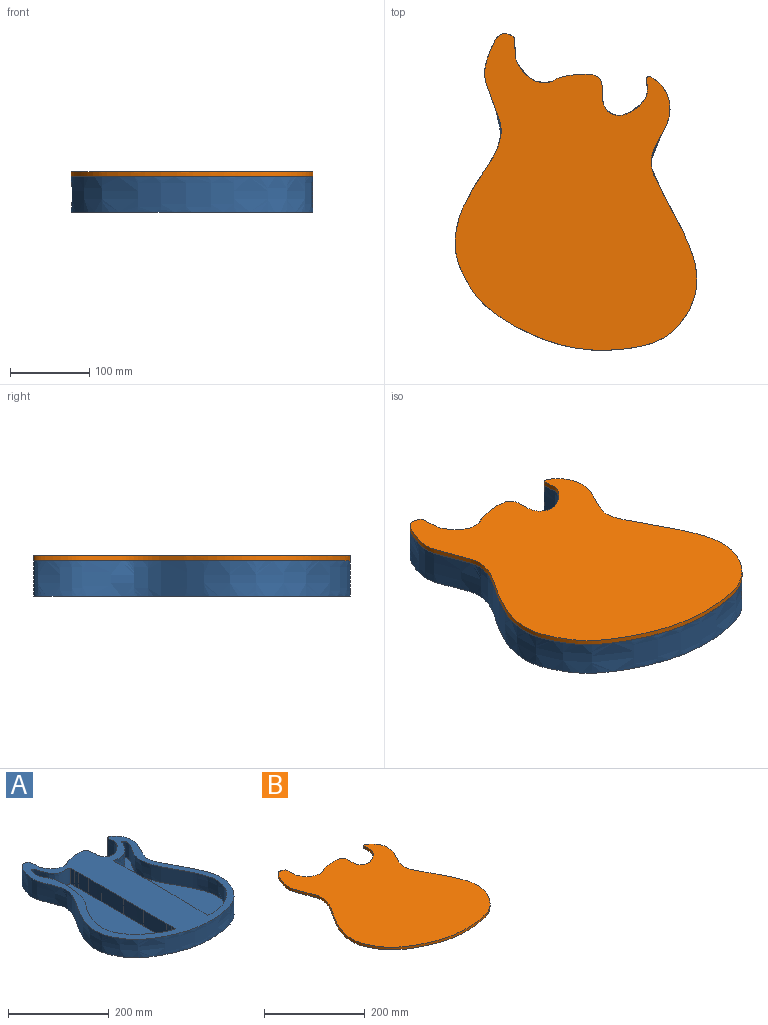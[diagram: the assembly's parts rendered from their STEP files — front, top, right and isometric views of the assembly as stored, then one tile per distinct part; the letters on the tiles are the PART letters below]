
ASSEMBLY  parts=2 mates=1
PART A: 21 faces, bbox 309.7x404x44.5 mm
  f0: plane 403.97x309.73mm, normal (0,0,1), area 41855.9mm2, adj f1,f3,f4,f5,f6,f7,f8,f10
  f1: extruded ~396.77x305.5mm, area 57898.6mm2, adj f0,f2
  f2: plane 403.97x309.73mm, normal (0,0,-1), area 81380.2mm2, adj f1
  f3: extruded ~38.1x13.88mm, area 530.3mm2, adj f0,f4,f8,f9
  f4: plane 38.1x11.9mm, normal (1,0,0), area 453.3mm2, adj f0,f3,f5,f9
  f5: extruded ~300.85x97.77mm, area 17424.5mm2, adj f0,f4,f6,f9
  f6: plane 38.1x23.8mm, normal (1,0,0), area 906.7mm2, adj f0,f5,f7,f9
  f7: extruded ~203.27x38.1mm, area 7747.2mm2, adj f0,f6,f8,f9
  f8: plane 38.1x9.92mm, normal (1,0,0), area 377.8mm2, adj f0,f3,f7,f9
  f9: plane 306.38x100.36mm, normal (0,0,1), area 18350.1mm2, adj f3,f4,f5,f6,f7,f8
  f10: plane 38.1x10.91mm, normal (-1,0,0), area 415.6mm2, adj f0,f11,f19,f20
  f11: extruded ~38.1x11.9mm, area 455.2mm2, adj f0,f10,f12,f20
  f12: plane 64.45x38.1mm, normal (-1,0,0), area 2455.6mm2, adj f0,f11,f13,f20
  f13: extruded ~56.88x38.1mm, area 2167.2mm2, adj f0,f12,f14,f20
  f14: plane 63.1x38.1mm, normal (-1,0,0), area 2404mm2, adj f0,f13,f15,f20
  f15: extruded ~38.1x35.52mm, area 1353.2mm2, adj f0,f14,f16,f20
  f16: plane 38.1x28.35mm, normal (-1,0,0), area 1080.3mm2, adj f0,f15,f17,f20
  f17: extruded ~38.1x10.13mm, area 387mm2, adj f0,f16,f18,f20
  f18: plane 38.1x11.28mm, normal (-1,0,0), area 429.7mm2, adj f0,f17,f19,f20
  f19: extruded ~344.12x100.4mm, area 18794.2mm2, adj f0,f10,f18,f20
  f20: plane 355.89x106.71mm, normal (0,0,1), area 21140.1mm2, adj f10,f11,f12,f13,f14,f15,f16,f17
PART B: 3 faces, bbox 309.7x404x6.4 mm
  f0: extruded ~396.77x305.5mm, area 8271.2mm2, adj f1,f2
  f1: plane 403.97x309.73mm, normal (0,0,1), area 81380.2mm2, adj f0
  f2: plane 403.97x309.73mm, normal (0,0,-1), area 81380.2mm2, adj f0
PLACE A t=(-24.44,-1.57,3.51)mm
PLACE B t=(-24.44,-1.57,47.96)mm
MATE parallel A.f0 <-> B.f2  axis (0,0,1) through (-95.19,-166.81,47.96)mm
